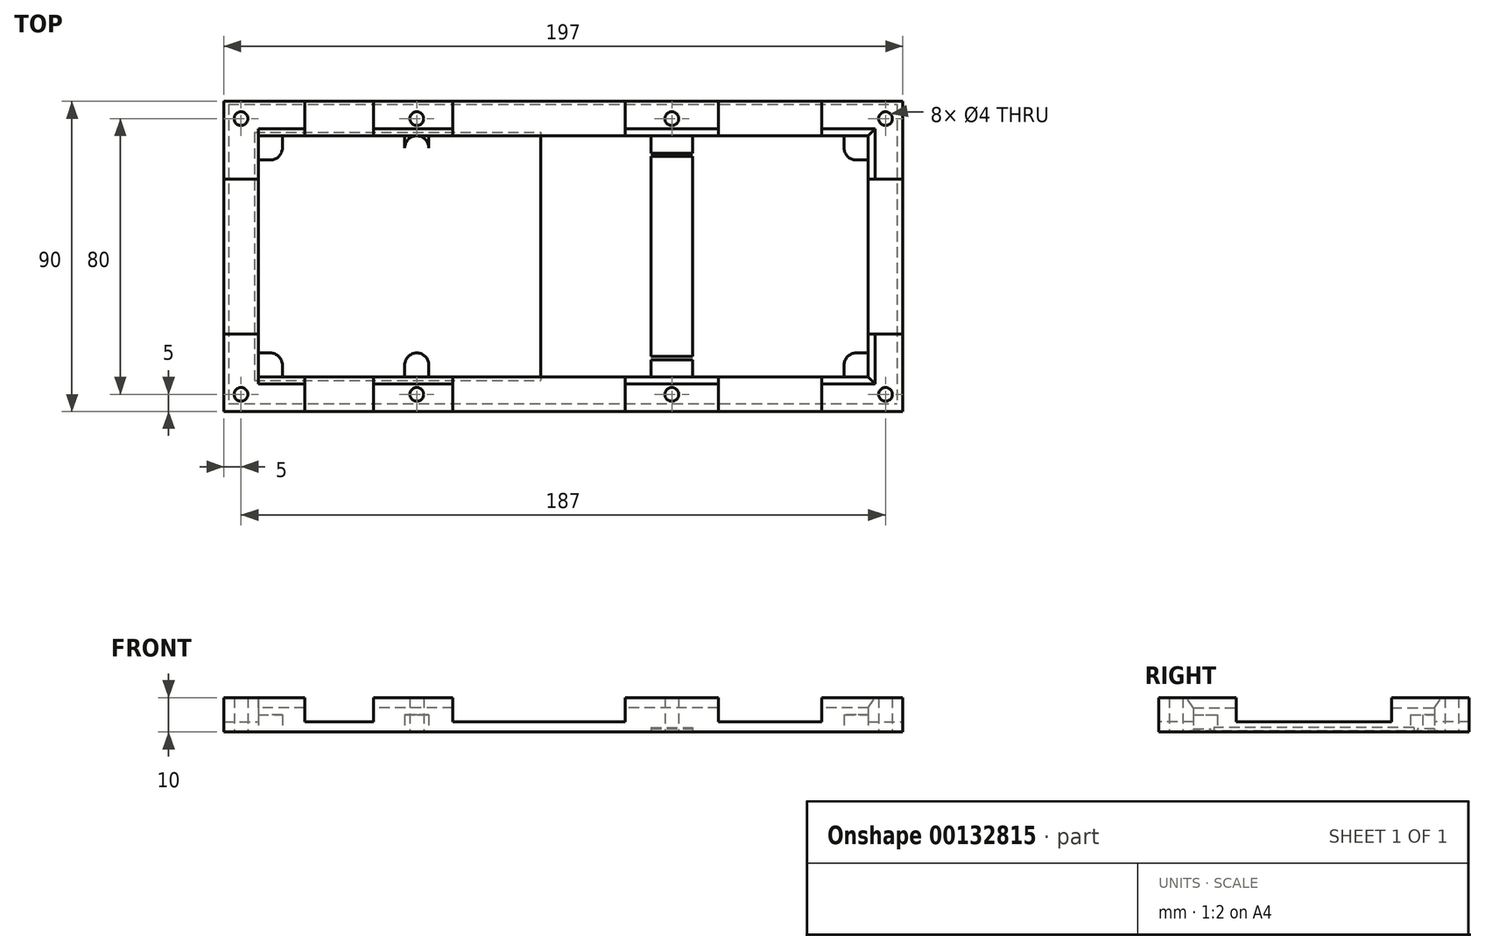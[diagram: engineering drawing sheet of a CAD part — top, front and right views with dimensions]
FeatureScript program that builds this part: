
annotation { "Feature Type Name" : "Feature", "Feature Type Description" : "" }
export const myFeature = defineFeature(function(context is Context, id is Id, definition is map)
    precondition{}
    {
        {
            var Q0;
            Q0=qCreatedBy(makeId("Top.planeOp"),FACE);
            var sketch = newSketch(context, id + "F0", { "sketchPlane" : qUnion([Q0])});
            skLineSegment(sketch, "E0.bottom", {"start": v(-88.5, -35) * mm, "end": v(88.5, -35) * mm});
            skLineSegment(sketch, "E0.top", {"start": v(-88.5, 35) * mm, "end": v(88.5, 35) * mm});
            skLineSegment(sketch, "E0.left", {"start": v(-88.5, -35) * mm, "end": v(-88.5, 35) * mm});
            skLineSegment(sketch, "E0.right", {"start": v(88.5, -35) * mm, "end": v(88.5, 35) * mm});
            skLineSegment(sketch, "E1.bottom", {"start": v(-98.5, 45) * mm, "end": v(98.5, 45) * mm});
            skLineSegment(sketch, "E1.top", {"start": v(-98.5, -45) * mm, "end": v(98.5, -45) * mm});
            skLineSegment(sketch, "E1.left", {"start": v(-98.5, 45) * mm, "end": v(-98.5, -45) * mm});
            skLineSegment(sketch, "E1.right", {"start": v(98.5, 45) * mm, "end": v(98.5, -45) * mm});
            skLineSegment(sketch, "E2", {"start": v(-81.5, -35) * mm, "end": v(-81.5, -31.5) * mm});
            skLineSegment(sketch, "E3", {"start": v(-88.5, -28) * mm, "end": v(-85, -28) * mm});
            skArc(sketch, "E4", {"start": v(-81.5, -31.5) * mm, "mid": v(-82.53, -29.03) * mm, "end": v(-85, -28) * mm});
            skArc(sketch, "E5.MirrorCS", {"start": v(-81.5, 31.5) * mm, "mid": v(-82.53, 29.03) * mm, "end": v(-85, 28) * mm});
            skLineSegment(sketch, "E6.MirrorCS", {"start": v(-88.5, 28) * mm, "end": v(-85, 28) * mm});
            skLineSegment(sketch, "E7.MirrorCS", {"start": v(-81.5, 35) * mm, "end": v(-81.5, 31.5) * mm});
            skLineSegment(sketch, "E8.MirrorCS", {"start": v(-88.5, 35) * mm, "end": v(-88.5, -35) * mm});
            skLineSegment(sketch, "E9.MirrorCS", {"start": v(81.5, -35) * mm, "end": v(81.5, -31.5) * mm});
            skArc(sketch, "E10.MirrorCS", {"start": v(81.5, -31.5) * mm, "mid": v(82.53, -29.03) * mm, "end": v(85, -28) * mm});
            skLineSegment(sketch, "E11.MirrorCS", {"start": v(88.5, -28) * mm, "end": v(85, -28) * mm});
            skArc(sketch, "E12.MirrorCS", {"start": v(81.5, 31.5) * mm, "mid": v(82.53, 29.03) * mm, "end": v(85, 28) * mm});
            skLineSegment(sketch, "E13.MirrorCS", {"start": v(88.5, 28) * mm, "end": v(85, 28) * mm});
            skLineSegment(sketch, "E14.MirrorCS", {"start": v(81.5, 35) * mm, "end": v(81.5, 31.5) * mm});
            skLineSegment(sketch, "E15", {"start": v(-42.5, -51.36) * mm, "end": v(-42.5, 52.9) * mm});
            skLineSegment(sketch, "E16", {"start": v(-46, -35) * mm, "end": v(-46, -31.35) * mm});
            skCircle(sketch, "E17", {"center": v(-42.5, -31.5) * mm, "radius": 3.5 * mm});
            skLineSegment(sketch, "E18.MirrorCS", {"start": v(-39, -35) * mm, "end": v(-39, -31.35) * mm});
            skLineSegment(sketch, "E19.MirrorCS", {"start": v(-46, 35) * mm, "end": v(-46, 31.35) * mm});
            skLineSegment(sketch, "E20.MirrorCS", {"start": v(-39, 35) * mm, "end": v(-39, 31.35) * mm});
            skCircle(sketch, "E21.MirrorC", {"center": v(-42.5, 31.5) * mm, "radius": 3.5 * mm});
            skCircle(sketch, "E22", {"center": v(-93.5, 40) * mm, "radius": 2 * mm});
            skCircle(sketch, "E23.MirrorC", {"center": v(93.5, 40) * mm, "radius": 2 * mm});
            skCircle(sketch, "E24.MirrorC", {"center": v(-93.5, -40) * mm, "radius": 2 * mm});
            skCircle(sketch, "E25.MirrorC", {"center": v(93.5, -40) * mm, "radius": 2 * mm});
            skLineSegment(sketch, "E26", {"start": v(31.5, 57.33) * mm, "end": v(31.5, -52.15) * mm});
            skCircle(sketch, "E27", {"center": v(-42.5, 40) * mm, "radius": 2 * mm});
            skCircle(sketch, "E28", {"center": v(31.5, 40) * mm, "radius": 2 * mm});
            skCircle(sketch, "E29.MirrorC", {"center": v(-42.5, -40) * mm, "radius": 2 * mm});
            skCircle(sketch, "E30.MirrorC", {"center": v(31.5, -40) * mm, "radius": 2 * mm});
            skSolve(sketch);
        }
        {
            var Q0;
            {var subQ0=sQuery(id+"F0.wireOp",EDGE,"E1.left");Q0=makeQuery(id+"F0.imprint","IMPRINT",FACE,{"disambiguationData":[TD([[makeQuery(id+"F0.imprint","IMPRINT",EDGE,{"derivedFrom":subQ0}),1.0]])]});}
            var Q1;
            {var subQ5=sQuery(id+"F0.wireOp",EDGE,"E1.right");Q1=makeQuery(id+"F0.imprint","IMPRINT",FACE,{"disambiguationData":[TD([[makeQuery(id+"F0.imprint","IMPRINT",EDGE,{"derivedFrom":subQ5}),-1.0]])]});}
            var Q2;
            {var subQ3=sQuery(id+"F0.wireOp",EDGE,"E0.top");var subQ9=makeQuery(id+"F0.imprint","INTERSECT",VERTEX,{"derivedFrom":[subQ3,sQuery(id+"F0.wireOp",EDGE,"E20.MirrorCS")]});Q2=makeQuery(id+"F0.imprint","IMPRINT",FACE,{"disambiguationData":[TD([[makeQuery(id+"F0.imprint","IMPRINT",EDGE,{"disambiguationData":[TD([[subQ9,-1.0]])],"derivedFrom":subQ3}),1.0]])]});}
            var Q3;
            {var subQ11=sQuery(id+"F0.wireOp",EDGE,"E0.bottom");var subQ12=makeQuery(id+"F0.imprint","INTERSECT",VERTEX,{"derivedFrom":[subQ11,sQuery(id+"F0.wireOp",EDGE,"E18.MirrorCS")]});Q3=makeQuery(id+"F0.imprint","IMPRINT",FACE,{"disambiguationData":[TD([[makeQuery(id+"F0.imprint","IMPRINT",EDGE,{"disambiguationData":[TD([[subQ12,-1.0]])],"derivedFrom":subQ11}),-1.0]])]});}
            extrude(context, id + "F1", {"entities" : qUnion([Q0, Q1, Q2, Q3]), "depth" : 10 * mm});
        }
        {
            var Q0;
            {var subQ1=sQuery(id+"F0.wireOp",EDGE,"E2");Q0=makeQuery(id+"F0.imprint","IMPRINT",FACE,{"disambiguationData":[TD([[makeQuery(id+"F0.imprint","IMPRINT",EDGE,{"derivedFrom":subQ1}),1.0]])]});}
            var Q1;
            {var subQ0=sQuery(id+"F0.wireOp",EDGE,"E16");var subQ1=sQuery(id+"F0.wireOp",EDGE,"E0.bottom");var subQ2=makeQuery(id+"F0.imprint","INTERSECT",VERTEX,{"derivedFrom":[subQ1,subQ0]});Q1=makeQuery(id+"F0.imprint","IMPRINT",FACE,{"disambiguationData":[TD([[makeQuery(id+"F0.imprint","IMPRINT",EDGE,{"disambiguationData":[TD([[subQ2,-1.0]])],"derivedFrom":subQ0}),-1.0]])]});}
            var Q2;
            {var subQ0=sQuery(id+"F0.wireOp",EDGE,"E18.MirrorCS");var subQ1=sQuery(id+"F0.wireOp",EDGE,"E0.bottom");var subQ2=makeQuery(id+"F0.imprint","INTERSECT",VERTEX,{"derivedFrom":[subQ1,subQ0]});Q2=makeQuery(id+"F0.imprint","IMPRINT",FACE,{"disambiguationData":[TD([[makeQuery(id+"F0.imprint","IMPRINT",EDGE,{"disambiguationData":[TD([[subQ2,-1.0]])],"derivedFrom":subQ0}),1.0]])]});}
            var Q3;
            {var subQ0=sQuery(id+"F0.wireOp",EDGE,"E17");var subQ4=makeQuery(id+"F0.imprint","INTERSECT",VERTEX,{"derivedFrom":[sQuery(id+"F0.wireOp",EDGE,"E16"),subQ0]});Q3=makeQuery(id+"F0.imprint","IMPRINT",FACE,{"disambiguationData":[TD([[makeQuery(id+"F0.imprint","IMPRINT",EDGE,{"disambiguationData":[TD([[subQ4,1.0]])],"derivedFrom":subQ0}),1.0]])]});}
            var Q4;
            {var subQ0=sQuery(id+"F0.wireOp",EDGE,"E17");var subQ4=makeQuery(id+"F0.imprint","INTERSECT",VERTEX,{"derivedFrom":[subQ0,sQuery(id+"F0.wireOp",EDGE,"E18.MirrorCS")]});Q4=makeQuery(id+"F0.imprint","IMPRINT",FACE,{"disambiguationData":[TD([[makeQuery(id+"F0.imprint","IMPRINT",EDGE,{"disambiguationData":[TD([[subQ4,-1.0]])],"derivedFrom":subQ0}),1.0]])]});}
            var Q5;
            {var subQ1=sQuery(id+"F0.wireOp",EDGE,"E6.MirrorCS");Q5=makeQuery(id+"F0.imprint","IMPRINT",FACE,{"disambiguationData":[TD([[makeQuery(id+"F0.imprint","IMPRINT",EDGE,{"derivedFrom":subQ1}),1.0]])]});}
            var Q6;
            {var subQ0=sQuery(id+"F0.wireOp",EDGE,"E21.MirrorC");var subQ4=makeQuery(id+"F0.imprint","INTERSECT",VERTEX,{"derivedFrom":[sQuery(id+"F0.wireOp",EDGE,"E20.MirrorCS"),subQ0]});Q6=makeQuery(id+"F0.imprint","IMPRINT",FACE,{"disambiguationData":[TD([[makeQuery(id+"F0.imprint","IMPRINT",EDGE,{"disambiguationData":[TD([[subQ4,-1.0]])],"derivedFrom":subQ0}),-1.0]])]});}
            var Q7;
            {var subQ0=sQuery(id+"F0.wireOp",EDGE,"E20.MirrorCS");var subQ1=sQuery(id+"F0.wireOp",EDGE,"E0.top");var subQ2=makeQuery(id+"F0.imprint","INTERSECT",VERTEX,{"derivedFrom":[subQ1,subQ0]});Q7=makeQuery(id+"F0.imprint","IMPRINT",FACE,{"disambiguationData":[TD([[makeQuery(id+"F0.imprint","IMPRINT",EDGE,{"disambiguationData":[TD([[subQ2,-1.0]])],"derivedFrom":subQ0}),-1.0]])]});}
            var Q8;
            {var subQ0=sQuery(id+"F0.wireOp",EDGE,"E19.MirrorCS");var subQ1=sQuery(id+"F0.wireOp",EDGE,"E0.top");var subQ2=makeQuery(id+"F0.imprint","INTERSECT",VERTEX,{"derivedFrom":[subQ1,subQ0]});Q8=makeQuery(id+"F0.imprint","IMPRINT",FACE,{"disambiguationData":[TD([[makeQuery(id+"F0.imprint","IMPRINT",EDGE,{"disambiguationData":[TD([[subQ2,-1.0]])],"derivedFrom":subQ0}),1.0]])]});}
            var Q9;
            {var subQ0=sQuery(id+"F0.wireOp",EDGE,"E21.MirrorC");var subQ4=makeQuery(id+"F0.imprint","INTERSECT",VERTEX,{"derivedFrom":[sQuery(id+"F0.wireOp",EDGE,"E19.MirrorCS"),subQ0]});Q9=makeQuery(id+"F0.imprint","IMPRINT",FACE,{"disambiguationData":[TD([[makeQuery(id+"F0.imprint","IMPRINT",EDGE,{"disambiguationData":[TD([[subQ4,1.0]])],"derivedFrom":subQ0}),-1.0]])]});}
            var Q10;
            {var subQ1=sQuery(id+"F0.wireOp",EDGE,"E9.MirrorCS");Q10=makeQuery(id+"F0.imprint","IMPRINT",FACE,{"disambiguationData":[TD([[makeQuery(id+"F0.imprint","IMPRINT",EDGE,{"derivedFrom":subQ1}),-1.0]])]});}
            var Q11;
            {var subQ4=sQuery(id+"F0.wireOp",EDGE,"E13.MirrorCS");Q11=makeQuery(id+"F0.imprint","IMPRINT",FACE,{"disambiguationData":[TD([[makeQuery(id+"F0.imprint","IMPRINT",EDGE,{"derivedFrom":subQ4}),-1.0]])]});}
            extrude(context, id + "F2", {"entities" : qUnion([Q0, Q1, Q2, Q3, Q4, Q5, Q6, Q7, Q8, Q9, Q10, Q11]), "operationType" : NewBodyOperationType.ADD, "depth" : 5 * mm});
        }
        {
            var Q0;
            Q0=makeQuery(id+"F1.opExtrude","CAP_EDGE",EDGE,{"disambiguationData":[OSD([sQuery(id+"F0.wireOp",EDGE,"E8.MirrorCS")])],"isStart":false});
            var Q1;
            Q1=makeQuery(id+"F1.opExtrude","CAP_EDGE",EDGE,{"disambiguationData":[OSD([sQuery(id+"F0.wireOp",EDGE,"E0.bottom")])],"isStart":false});
            var Q2;
            Q2=makeQuery(id+"F1.opExtrude","CAP_EDGE",EDGE,{"disambiguationData":[OSD([sQuery(id+"F0.wireOp",EDGE,"E0.right")])],"isStart":false});
            var Q3;
            Q3=makeQuery(id+"F1.opExtrude","CAP_EDGE",EDGE,{"disambiguationData":[OSD([sQuery(id+"F0.wireOp",EDGE,"E0.top")])],"isStart":false});
            chamfer(context, id + "F3", {"entities" : qUnion([Q0, Q1, Q2, Q3]), "chamferType" : ChamferType.TWO_OFFSETS, "width1" : 3 * mm, "oppositeDirection" : false, "width2" : 2 * mm, "tangentPropagation" : true});
        }
        {
            var Q0;
            Q0=qCreatedBy(makeId("Top.planeOp"),FACE);
            var sketch = newSketch(context, id + "F4", { "sketchPlane" : qUnion([Q0])});
            skLineSegment(sketch, "E31.bottom", {"start": v(25.5, 29) * mm, "end": v(37.5, 29) * mm});
            skLineSegment(sketch, "E31.top", {"start": v(25.5, -29) * mm, "end": v(37.5, -29) * mm});
            skLineSegment(sketch, "E31.left", {"start": v(25.5, 29) * mm, "end": v(25.5, -29) * mm});
            skLineSegment(sketch, "E31.right", {"start": v(37.5, 29) * mm, "end": v(37.5, -29) * mm});
            skSolve(sketch);
        }
        {
            var Q0;
            Q0=makeQuery(id+"F4.imprint","IMPRINT",FACE,{"disambiguationData":[TD([[makeQuery(id+"F4.imprint","IMPRINT",EDGE,{"derivedFrom":sQuery(id+"F4.wireOp",EDGE,"E31.bottom")}),-1.0]])]});
            extrude(context, id + "F5", {"entities" : qUnion([Q0]), "depth" : 1.3 * mm});
        }
        {
            var Q0;
            Q0=qCreatedBy(makeId("Top.planeOp"),FACE);
            var sketch = newSketch(context, id + "F6", { "sketchPlane" : qUnion([Q0])});
            skLineSegment(sketch, "E32.bottom", {"start": v(-75, 53.01) * mm, "end": v(-55, 53.01) * mm});
            skLineSegment(sketch, "E32.top", {"start": v(-75, -49.04) * mm, "end": v(-55, -49.04) * mm});
            skLineSegment(sketch, "E32.left", {"start": v(-75, 53.01) * mm, "end": v(-75, -49.04) * mm});
            skLineSegment(sketch, "E32.right", {"start": v(-55, 53.01) * mm, "end": v(-55, -49.04) * mm});
            skLineSegment(sketch, "E33.bottom", {"start": v(-32, 53.41) * mm, "end": v(18, 53.41) * mm});
            skLineSegment(sketch, "E33.top", {"start": v(-32, -49.04) * mm, "end": v(18, -49.04) * mm});
            skLineSegment(sketch, "E33.left", {"start": v(-32, 53.41) * mm, "end": v(-32, -49.04) * mm});
            skLineSegment(sketch, "E33.right", {"start": v(18, 53.41) * mm, "end": v(18, -49.04) * mm});
            skLineSegment(sketch, "E34.bottom", {"start": v(45, 53.09) * mm, "end": v(75, 53.09) * mm});
            skLineSegment(sketch, "E34.top", {"start": v(45, -50.36) * mm, "end": v(75, -50.36) * mm});
            skLineSegment(sketch, "E34.left", {"start": v(45, 53.09) * mm, "end": v(45, -50.36) * mm});
            skLineSegment(sketch, "E34.right", {"start": v(75, 53.09) * mm, "end": v(75, -50.36) * mm});
            skLineSegment(sketch, "E35.bottom", {"start": v(-113.4, 22.5) * mm, "end": v(107.06, 22.5) * mm});
            skLineSegment(sketch, "E35.top", {"start": v(-113.4, -22.5) * mm, "end": v(107.06, -22.5) * mm});
            skLineSegment(sketch, "E35.left", {"start": v(-113.4, 22.5) * mm, "end": v(-113.4, -22.5) * mm});
            skLineSegment(sketch, "E35.right", {"start": v(107.06, 22.5) * mm, "end": v(107.06, -22.5) * mm});
            skSolve(sketch);
        }
        {
            var Q0;
            Q0=qSketchRegion(id+"F6",true);
            extrude(context, id + "F7", {"entities" : qUnion([Q0]), "operationType" : NewBodyOperationType.REMOVE, "depth" : 25 * mm, "hasSecondDirection" : true, "secondDirectionOppositeDirection" : false, "secondDirectionDepth" : 3 * mm});
        }
        {
            var Q0;
            Q0=qCreatedBy(makeId("Top.planeOp"),FACE);
            var sketch = newSketch(context, id + "F8", { "sketchPlane" : qUnion([Q0])});
            skLineSegment(sketch, "E36.bottom", {"start": v(25.5, 35) * mm, "end": v(37.5, 35) * mm});
            skLineSegment(sketch, "E36.top", {"start": v(25.5, 30) * mm, "end": v(37.5, 30) * mm});
            skLineSegment(sketch, "E36.left", {"start": v(25.5, 35) * mm, "end": v(25.5, 30) * mm});
            skLineSegment(sketch, "E36.right", {"start": v(37.5, 35) * mm, "end": v(37.5, 30) * mm});
            skPoint(sketch, "E37.firstSnap0", {"position": v(37.5, 32.5) * mm});
            skLineSegment(sketch, "E38.MirrorCS", {"start": v(37.5, -35) * mm, "end": v(37.5, -30) * mm});
            skLineSegment(sketch, "E39.MirrorCS", {"start": v(25.5, -35) * mm, "end": v(37.5, -35) * mm});
            skPoint(sketch, "E40.MirrorP", {"position": v(37.5, -32.5) * mm});
            skLineSegment(sketch, "E41.MirrorCS", {"start": v(25.5, -30) * mm, "end": v(37.5, -30) * mm});
            skLineSegment(sketch, "E42.MirrorCS", {"start": v(25.5, -35) * mm, "end": v(25.5, -30) * mm});
            skSolve(sketch);
        }
        {
            var Q0;
            Q0=makeQuery(id+"F8.imprint","IMPRINT",FACE,{"disambiguationData":[TD([[makeQuery(id+"F8.imprint","IMPRINT",EDGE,{"derivedFrom":sQuery(id+"F8.wireOp",EDGE,"E36.bottom")}),-1.0]])]});
            var Q1;
            Q1=makeQuery(id+"F8.imprint","IMPRINT",FACE,{"disambiguationData":[TD([[makeQuery(id+"F8.imprint","IMPRINT",EDGE,{"derivedFrom":sQuery(id+"F8.wireOp",EDGE,"E38.MirrorCS")}),1.0]])]});
            extrude(context, id + "F9", {"entities" : qUnion([Q0, Q1]), "operationType" : NewBodyOperationType.ADD, "depth" : 1 * mm});
        }
        {
            var Q0;
            Q0=qCreatedBy(makeId("Top.planeOp"),FACE);
            var sketch = newSketch(context, id + "F10", { "sketchPlane" : qUnion([Q0])});
            skLineSegment(sketch, "E43.bottom", {"start": v(-89.6, 36) * mm, "end": v(-6.5, 36) * mm});
            skLineSegment(sketch, "E43.top", {"start": v(-89.6, -36) * mm, "end": v(-6.5, -36) * mm});
            skLineSegment(sketch, "E43.left", {"start": v(-89.6, 36) * mm, "end": v(-89.6, -36) * mm});
            skLineSegment(sketch, "E43.right", {"start": v(-6.5, 36) * mm, "end": v(-6.5, -36) * mm});
            skSolve(sketch);
        }
        {
            var Q0;
            Q0=qSketchRegion(id+"F10",true);
            extrude(context, id + "F11", {"entities" : qUnion([Q0]), "depth" : 0.3 * mm});
        }
        {
            var Q0;
            Q0=qCreatedBy(makeId("Top.planeOp"),FACE);
            var sketch = newSketch(context, id + "F12", { "sketchPlane" : qUnion([Q0])});
            skLineSegment(sketch, "E44.bottom", {"start": v(-97.11, 44.15) * mm, "end": v(96.78, 44.15) * mm});
            skLineSegment(sketch, "E44.top", {"start": v(-97.11, -42.68) * mm, "end": v(96.78, -42.68) * mm});
            skLineSegment(sketch, "E44.left", {"start": v(-97.11, 44.15) * mm, "end": v(-97.11, -42.68) * mm});
            skLineSegment(sketch, "E44.right", {"start": v(96.78, 44.15) * mm, "end": v(96.78, -42.68) * mm});
            skSolve(sketch);
        }
        {
            var Q0;
            Q0=qSketchRegion(id+"F12",true);
            extrude(context, id + "F13", {"entities" : qUnion([Q0]), "depth" : 0.01 * mm});
        }
    });
